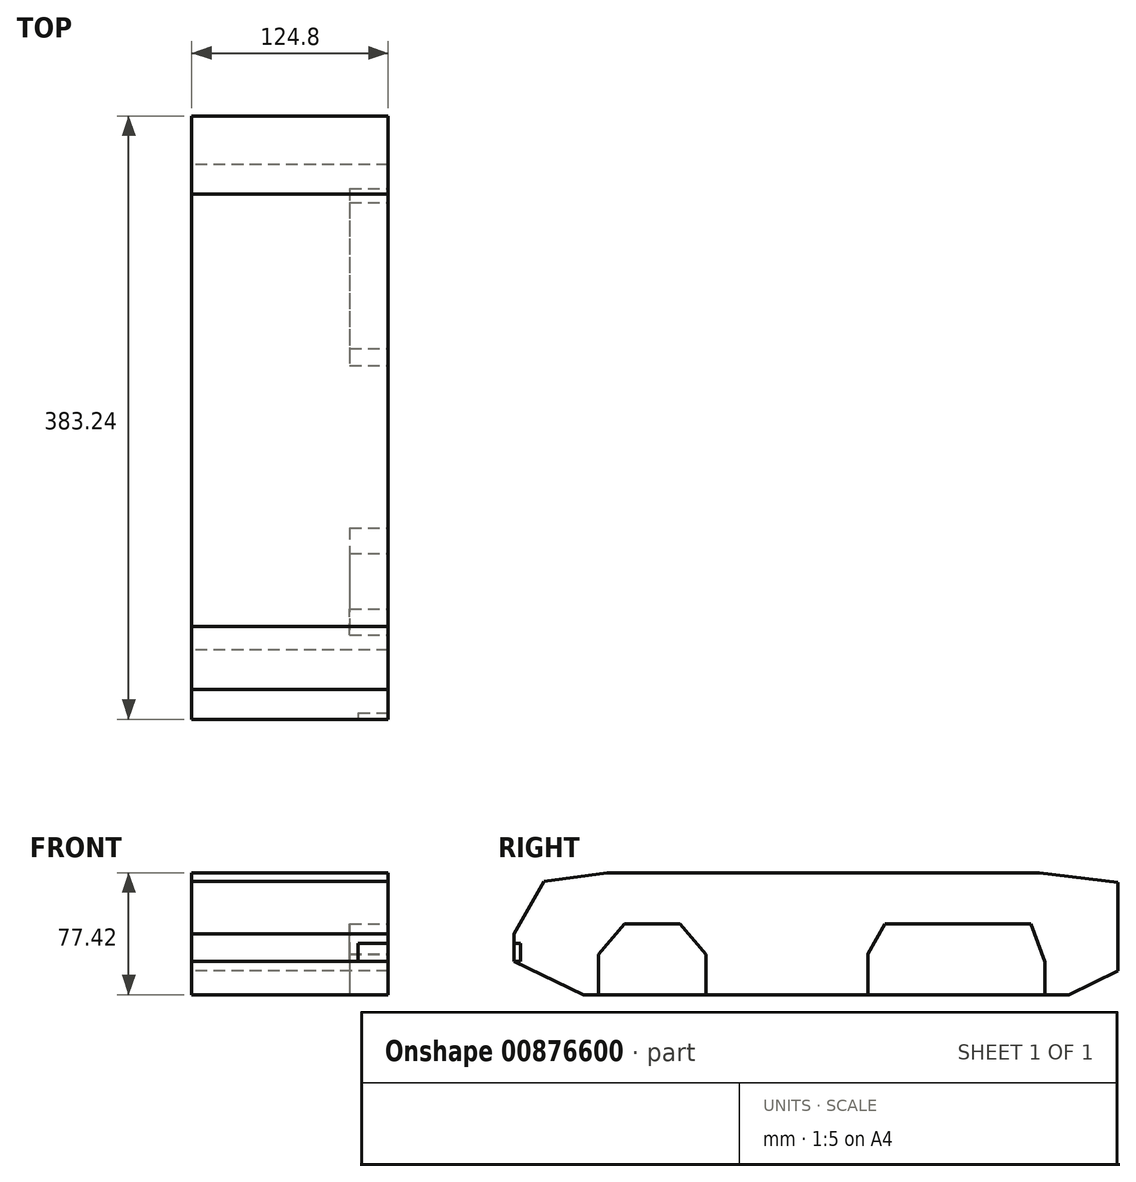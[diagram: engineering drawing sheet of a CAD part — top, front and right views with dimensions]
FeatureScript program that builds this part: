
annotation { "Feature Type Name" : "Feature", "Feature Type Description" : "" }
export const myFeature = defineFeature(function(context is Context, id is Id, definition is map)
    precondition{}
    {
        {
            var Q0;
            Q0=qCreatedBy(makeId("Right.planeOp"),FACE);
            var sketch = newSketch(context, id + "F0", { "sketchPlane" : qUnion([Q0])});
            skLineSegment(sketch, "E0", {"start": v(-7.48, -0.03) * mm, "end": v(-7.48, -28.35) * mm});
            skLineSegment(sketch, "E1", {"start": v(4.95, -12.89) * mm, "end": v(92.35, -12.89) * mm});
            skLineSegment(sketch, "E2", {"start": v(92.35, -12.89) * mm, "end": v(258.4, -12.89) * mm});
            skLineSegment(sketch, "E3", {"start": v(258.4, -12.89) * mm, "end": v(314.8, -12.89) * mm});
            skLineSegment(sketch, "E4", {"start": v(314.8, -12.89) * mm, "end": v(389.06, -12.89) * mm});
            skLineSegment(sketch, "E5", {"start": v(5.76, 54.65) * mm, "end": v(24.64, 87.74) * mm});
            skLineSegment(sketch, "E6", {"start": v(24.64, 87.74) * mm, "end": v(64.82, 93.36) * mm});
            skLineSegment(sketch, "E7", {"start": v(64.82, 93.36) * mm, "end": v(339.38, 93.36) * mm});
            skLineSegment(sketch, "E8", {"start": v(339.38, 93.36) * mm, "end": v(389, 87.26) * mm});
            skLineSegment(sketch, "E9", {"start": v(389, 87.26) * mm, "end": v(389, 31.09) * mm});
            skLineSegment(sketch, "E10", {"start": v(389, 31.09) * mm, "end": v(358.16, 15.94) * mm});
            skLineSegment(sketch, "E11", {"start": v(358.16, 15.94) * mm, "end": v(49.76, 15.94) * mm});
            skLineSegment(sketch, "E12", {"start": v(5.76, 37.08) * mm, "end": v(49.76, 15.94) * mm});
            skLineSegment(sketch, "E13", {"start": v(5.76, 37.08) * mm, "end": v(5.76, 54.65) * mm});
            skSolve(sketch);
        }
        {
            var Q0;
            Q0=makeQuery(id+"F0.imprint","IMPRINT",FACE,{"disambiguationData":[TD([[makeQuery(id+"F0.imprint","IMPRINT",EDGE,{"derivedFrom":sQuery(id+"F0.wireOp",EDGE,"E5")}),-1.0]])]});
            extrude(context, id + "F1", {"entities" : qUnion([Q0]), "depth" : 62.4 * mm, "offsetDistance" : 25 * mm});
        }
        {
            var Q0;
            Q0=makeQuery(id+"F1.opExtrude","SWEPT_BODY",BODY,{"disambiguationData":[OSD([sQuery(id+"F0.wireOp",EDGE,"E5"),sQuery(id+"F0.wireOp",EDGE,"E6"),sQuery(id+"F0.wireOp",EDGE,"E7"),sQuery(id+"F0.wireOp",EDGE,"E8"),sQuery(id+"F0.wireOp",EDGE,"E9"),sQuery(id+"F0.wireOp",EDGE,"E10"),sQuery(id+"F0.wireOp",EDGE,"E11"),sQuery(id+"F0.wireOp",EDGE,"E12"),sQuery(id+"F0.wireOp",EDGE,"E13")])]});
            var Q1;
            Q1=qCreatedBy(makeId("Right.planeOp"),FACE);
            mirror(context, id + "F2", {"operationType" : NewBodyOperationType.ADD, "entities" : qUnion([Q0]), "mirrorPlane" : qUnion([Q1])});
        }
        {
            var Q0;
            Q0=makeQuery(id+"F1.opExtrude","CAP_FACE",FACE,{"disambiguationData":[OSD([sQuery(id+"F0.wireOp",EDGE,"E5"),sQuery(id+"F0.wireOp",EDGE,"E6"),sQuery(id+"F0.wireOp",EDGE,"E7"),sQuery(id+"F0.wireOp",EDGE,"E8"),sQuery(id+"F0.wireOp",EDGE,"E9"),sQuery(id+"F0.wireOp",EDGE,"E10"),sQuery(id+"F0.wireOp",EDGE,"E11"),sQuery(id+"F0.wireOp",EDGE,"E12"),sQuery(id+"F0.wireOp",EDGE,"E13"),sQuery(id+"F0.wireOp",EDGE,"4wLSxoU1-wjTP-RjS8-Fil5-mWYNnqUWUP30"),sQuery(id+"F0.wireOp",EDGE,"48A6rpqG-CFbU-eRET-mKrZ-eJfsxVEV9SlA"),sQuery(id+"F0.wireOp",EDGE,"mJXu88v2-1c1H-beHH-SZoW-kNSsEP4OQlNw"),sQuery(id+"F0.wireOp",EDGE,"9zfjlp77-5DH1-ibxi-NsB7-xBXRrqJBet8q"),sQuery(id+"F0.wireOp",EDGE,"EAvfL65t-ws5G-z6HX-9b2y-41olgLscPThn"),sQuery(id+"F0.wireOp",EDGE,"woMchWLh-lngx-aGm0-zVi9-AW22XXV3rjRF"),sQuery(id+"F0.wireOp",EDGE,"OjkRvJ6f-TrQS-QE7k-SG7G-hGT3ttrmzNO2"),sQuery(id+"F0.wireOp",EDGE,"GJGCzBqD-je1m-H5xu-PpAI-N9j6EvuqNyu1"),sQuery(id+"F0.wireOp",EDGE,"qaDVjuT4-XXzc-TGmE-cbP5-38UKHHHm1Y8I"),sQuery(id+"F0.wireOp",EDGE,"4253e018-d76d-4f98-b304-5639b9a294a90.MirrorCS"),sQuery(id+"F0.wireOp",EDGE,"15cb281f-81a5-4669-bf0f-18b36f5971e20.MirrorCS")])],"isStart":false});
            var sketch = newSketch(context, id + "F3", { "sketchPlane" : qUnion([Q0])});
            skLineSegment(sketch, "E14", {"start": v(342.79, 15.94) * mm, "end": v(230.52, 15.94) * mm});
            skLineSegment(sketch, "E15", {"start": v(342.79, 36.72) * mm, "end": v(333.98, 60.8) * mm});
            skLineSegment(sketch, "E16", {"start": v(333.98, 60.8) * mm, "end": v(241.13, 60.8) * mm});
            skLineSegment(sketch, "E17", {"start": v(241.13, 60.8) * mm, "end": v(230.52, 41.88) * mm});
            skLineSegment(sketch, "E18", {"start": v(230.52, 41.88) * mm, "end": v(230.52, 15.94) * mm});
            skLineSegment(sketch, "E19", {"start": v(127.4, 41.5) * mm, "end": v(127.4, 15.94) * mm});
            skLineSegment(sketch, "E20", {"start": v(127.4, 41.5) * mm, "end": v(110.94, 60.8) * mm});
            skLineSegment(sketch, "E21", {"start": v(110.94, 60.8) * mm, "end": v(75.7, 60.8) * mm});
            skLineSegment(sketch, "E22.MirrorCS", {"start": v(59.24, 41.5) * mm, "end": v(75.7, 60.8) * mm});
            skLineSegment(sketch, "E23.MirrorCS", {"start": v(59.24, 41.5) * mm, "end": v(59.24, 15.94) * mm});
            skLineSegment(sketch, "E24", {"start": v(342.79, 36.72) * mm, "end": v(342.79, 15.94) * mm});
            skLineSegment(sketch, "E25.trimOffspring", {"start": v(127.4, 15.94) * mm, "end": v(59.24, 15.94) * mm});
            skSolve(sketch);
        }
        {
            var Q0;
            Q0=makeQuery(id+"F3.imprint","IMPRINT",FACE,{"disambiguationData":[TD([[makeQuery(id+"F3.imprint","IMPRINT",EDGE,{"derivedFrom":sQuery(id+"F3.wireOp",EDGE,"E19")}),-1.0]])]});
            var Q1;
            Q1=makeQuery(id+"F3.imprint","IMPRINT",FACE,{"disambiguationData":[TD([[makeQuery(id+"F3.imprint","IMPRINT",EDGE,{"derivedFrom":sQuery(id+"F3.wireOp",EDGE,"E14")}),-1.0]])]});
            extrude(context, id + "F4", {"entities" : qUnion([Q0, Q1]), "operationType" : NewBodyOperationType.REMOVE, "depth" : -24.5 * mm, "offsetDistance" : 25 * mm});
        }
        {
            var Q0;
            {var subQ0=makeQuery(id+"F1.opExtrude","SWEPT_FACE",FACE,{"disambiguationData":[OSD([sQuery(id+"F0.wireOp",EDGE,"E13")])]});Q0=makeQuery(id+"F2.boolean.opBoolean","MERGE",FACE,{"derivedFrom":[subQ0,makeQuery(id+"F2.opPattern","COPY",FACE,{"derivedFrom":subQ0,"instanceName":"1"})]});}
            var sketch = newSketch(context, id + "F5", { "sketchPlane" : qUnion([Q0])});
            skLineSegment(sketch, "E26.bottom", {"start": v(43.35, 48.36) * mm, "end": v(62.4, 48.36) * mm});
            skLineSegment(sketch, "E26.right", {"start": v(62.4, 48.36) * mm, "end": v(62.4, 37.08) * mm});
            skLineSegment(sketch, "E27.left", {"start": v(62.4, 37.08) * mm, "end": v(62.4, 34.2) * mm});
            skLineSegment(sketch, "E28", {"start": v(62.4, 34.2) * mm, "end": v(62.4, 37.08) * mm});
            skPoint(sketch, "E29.orphan", {"position": v(43.35, 37.08) * mm});
            skLineSegment(sketch, "E30", {"start": v(43.35, 48.36) * mm, "end": v(43.35, 34.2) * mm});
            skLineSegment(sketch, "E31", {"start": v(43.35, 34.2) * mm, "end": v(62.4, 34.2) * mm});
            skLineSegment(sketch, "E32.bottom", {"start": v(11.67, 43.81) * mm, "end": v(22.82, 43.81) * mm});
            skLineSegment(sketch, "E32.top", {"start": v(11.67, 32.22) * mm, "end": v(22.82, 32.22) * mm});
            skLineSegment(sketch, "E32.left", {"start": v(11.67, 43.81) * mm, "end": v(11.67, 32.22) * mm});
            skLineSegment(sketch, "E32.right", {"start": v(22.82, 43.81) * mm, "end": v(22.82, 32.22) * mm});
            skSolve(sketch);
        }
        {
            var Q0;
            {var subQ0=sQuery(id+"F5.wireOp",EDGE,"E26.bottom");Q0=makeQuery(id+"F5.imprint","IMPRINT",FACE,{"disambiguationData":[TD([[makeQuery(id+"F5.imprint","IMPRINT",EDGE,{"derivedFrom":subQ0}),-1.0]])]});}
            var Q1;
            {var subQ0=sQuery(id+"F5.wireOp",EDGE,"E28");Q1=makeQuery(id+"F5.imprint","IMPRINT",FACE,{"disambiguationData":[TD([[makeQuery(id+"F5.imprint","IMPRINT",EDGE,{"derivedFrom":subQ0}),1.0]])]});}
            extrude(context, id + "F6", {"entities" : qUnion([Q0, Q1]), "operationType" : NewBodyOperationType.REMOVE, "oppositeDirection" : true, "depth" : 4.1 * mm, "offsetDistance" : 25 * mm});
        }
    });
